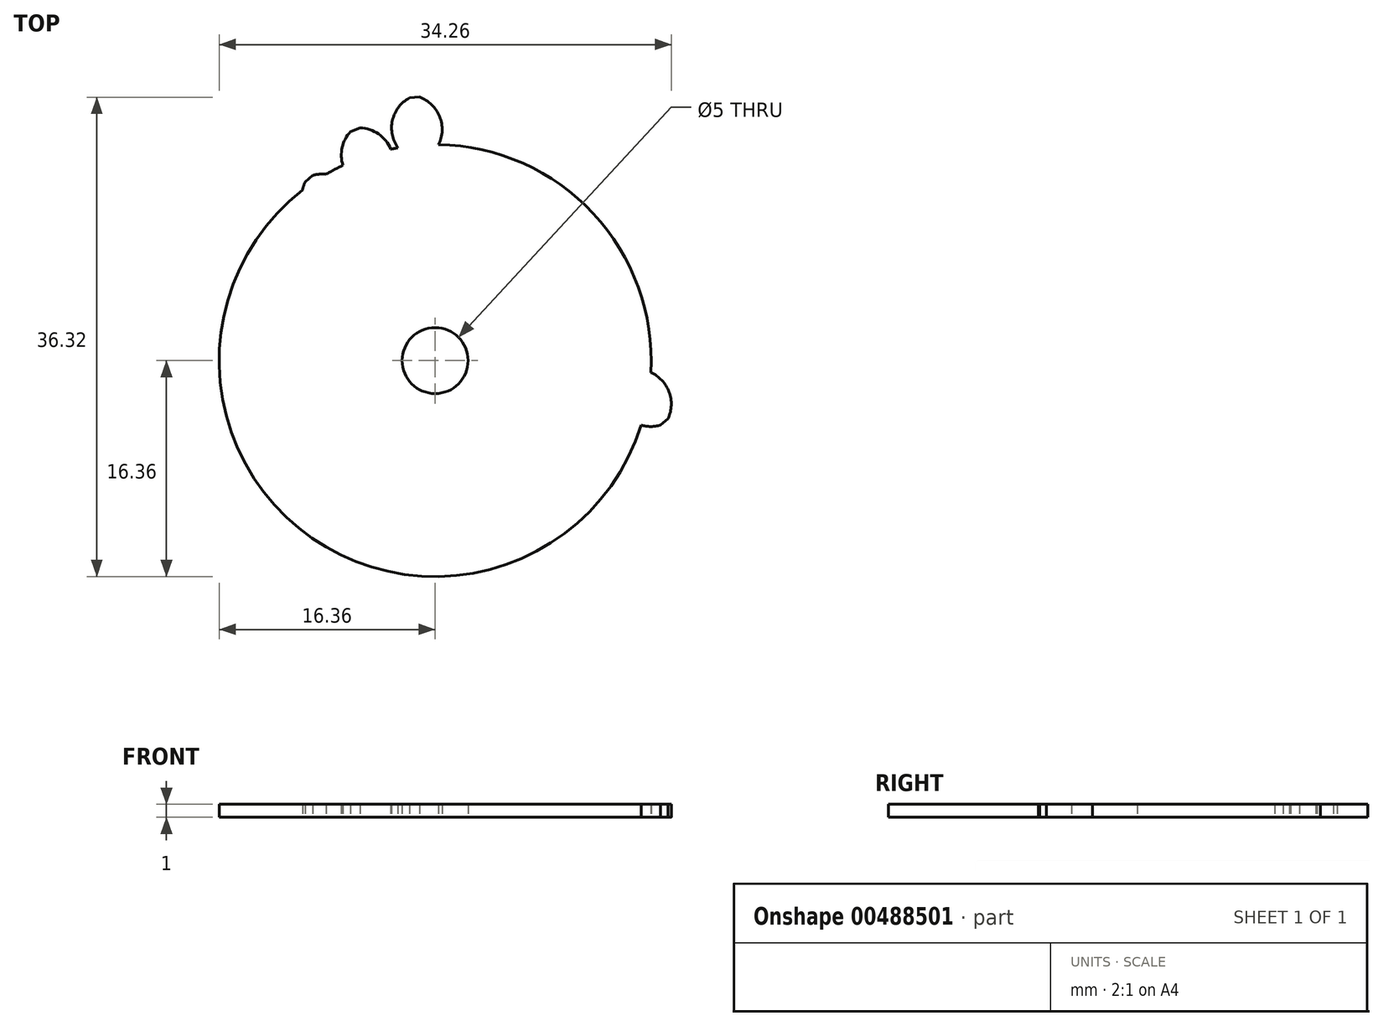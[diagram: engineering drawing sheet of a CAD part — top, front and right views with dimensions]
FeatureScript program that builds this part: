
annotation { "Feature Type Name" : "Feature", "Feature Type Description" : "" }
export const myFeature = defineFeature(function(context is Context, id is Id, definition is map)
    precondition{}
    {
        {
            assignVariable(context, id + "F0", {"name" : "GearDepth", "anyValue" : 1});
        }
        {
            var Q0;
            Q0=qCreatedBy(makeId("Top.planeOp"),FACE);
            var sketch = newSketch(context, id + "F1", { "sketchPlane" : qUnion([Q0])});
            skCircle(sketch, "E0", {"center": v(0, 0) * mm, "radius": 16.36 * mm});
            skCircle(sketch, "E1", {"center": v(0, 0) * mm, "radius": 18.18 * mm, "construction": true});
            skCircle(sketch, "E2", {"center": v(0, 0) * mm, "radius": 20 * mm, "construction": true});
            skLineSegment(sketch, "E3", {"start": v(0, 0) * mm, "end": v(0, 17.6) * mm, "construction": true});
            skLineSegment(sketch, "E4", {"start": v(0, 0) * mm, "end": v(-1.42, 18) * mm, "construction": true});
            skLineSegment(sketch, "E5", {"start": v(0, 18.18) * mm, "end": v(-10.54, 18.18) * mm, "construction": true});
            skLineSegment(sketch, "E6", {"start": v(0, 18.18) * mm, "end": v(-10.3, 14.44) * mm, "construction": true});
            skCircle(sketch, "E7", {"center": v(0, 18.18) * mm, "radius": 4.55 * mm, "construction": true});
            skCircle(sketch, "E8", {"center": v(-4.27, 16.63) * mm, "radius": 4.55 * mm, "construction": true});
            skArc(sketch, "E9", {"start": v(-8.54, 18.18) * mm, "mid": v(-8.56, 18.12) * mm, "end": v(-8.58, 18.06) * mm});
            skArc(sketch, "E10.trimOffspring", {"start": v(0.27, 16.36) * mm, "mid": v(0.34, 18.49) * mm, "end": v(-1.19, 19.96) * mm});
            skArc(sketch, "E11.MirrorCS", {"start": v(-2.82, 16.12) * mm, "mid": v(-3.23, 18.2) * mm, "end": v(-1.95, 19.9) * mm});
            skLineSegment(sketch, "E12", {"start": v(-1.95, 19.9) * mm, "end": v(-1.19, 19.96) * mm});
            skArc(sketch, "E13.1.0", {"start": v(-3.2, 14.66) * mm, "mid": v(-3.78, 16.7) * mm, "end": v(-5.7, 17.64) * mm});
            skLineSegment(sketch, "E13.1.1", {"start": v(-6.4, 17.34) * mm, "end": v(-5.7, 17.64) * mm});
            skArc(sketch, "E13.1.2", {"start": v(-6.06, 13.47) * mm, "mid": v(-7.1, 15.33) * mm, "end": v(-6.4, 17.34) * mm});
            skArc(sketch, "E13.2.0", {"start": v(-5.97, 11.97) * mm, "mid": v(-7.16, 13.74) * mm, "end": v(-9.26, 14.03) * mm});
            skLineSegment(sketch, "E13.2.1", {"start": v(-9.85, 13.53) * mm, "end": v(-9.26, 14.03) * mm});
            skArc(sketch, "E13.2.2", {"start": v(-8.33, 9.96) * mm, "mid": v(-9.88, 11.4) * mm, "end": v(-9.85, 13.53) * mm});
            skArc(sketch, "E13.3.0", {"start": v(-7.77, 8.56) * mm, "mid": v(-9.45, 9.87) * mm, "end": v(-11.54, 9.5) * mm});
            skLineSegment(sketch, "E13.3.1", {"start": v(-11.94, 8.85) * mm, "end": v(-11.54, 9.5) * mm});
            skArc(sketch, "E13.3.2", {"start": v(-9.4, 5.92) * mm, "mid": v(-11.32, 6.81) * mm, "end": v(-11.94, 8.85) * mm});
            skArc(sketch, "E13.4.0", {"start": v(-8.44, 4.76) * mm, "mid": v(-10.43, 5.48) * mm, "end": v(-12.31, 4.49) * mm});
            skLineSegment(sketch, "E13.4.1", {"start": v(-12.5, 3.74) * mm, "end": v(-12.31, 4.49) * mm});
            skArc(sketch, "E13.4.2", {"start": v(-9.16, 1.74) * mm, "mid": v(-11.27, 2) * mm, "end": v(-12.5, 3.74) * mm});
            skArc(sketch, "E13.5.0", {"start": v(-7.89, 0.93) * mm, "mid": v(-10.01, 1) * mm, "end": v(-11.5, -0.52) * mm});
            skLineSegment(sketch, "E13.5.1", {"start": v(-11.43, -1.29) * mm, "end": v(-11.5, -0.52) * mm});
            skArc(sketch, "E13.5.2", {"start": v(-7.65, -2.16) * mm, "mid": v(-9.73, -2.56) * mm, "end": v(-11.43, -1.29) * mm});
            skArc(sketch, "E13.6.0", {"start": v(-6.19, -2.53) * mm, "mid": v(-8.23, -3.12) * mm, "end": v(-9.17, -5.03) * mm});
            skLineSegment(sketch, "E13.6.1", {"start": v(-8.87, -5.74) * mm, "end": v(-9.17, -5.03) * mm});
            skArc(sketch, "E13.6.2", {"start": v(-5, -5.4) * mm, "mid": v(-6.86, -6.43) * mm, "end": v(-8.87, -5.74) * mm});
            skArc(sketch, "E13.7.0", {"start": v(-3.5, -5.3) * mm, "mid": v(-5.26, -6.5) * mm, "end": v(-5.56, -8.6) * mm});
            skLineSegment(sketch, "E13.7.1", {"start": v(-5.06, -9.18) * mm, "end": v(-5.56, -8.6) * mm});
            skArc(sketch, "E13.7.2", {"start": v(-1.49, -7.66) * mm, "mid": v(-2.94, -9.22) * mm, "end": v(-5.06, -9.18) * mm});
            skArc(sketch, "E13.8.0", {"start": v(-0.09, -7.1) * mm, "mid": v(-1.4, -8.78) * mm, "end": v(-1.03, -10.88) * mm});
            skLineSegment(sketch, "E13.8.1", {"start": v(-0.37, -11.28) * mm, "end": v(-1.03, -10.88) * mm});
            skArc(sketch, "E13.8.2", {"start": v(2.56, -8.73) * mm, "mid": v(1.66, -10.65) * mm, "end": v(-0.37, -11.28) * mm});
            skArc(sketch, "E13.9.0", {"start": v(3.72, -7.77) * mm, "mid": v(2.99, -9.77) * mm, "end": v(3.98, -11.64) * mm});
            skLineSegment(sketch, "E13.9.1", {"start": v(4.73, -11.82) * mm, "end": v(3.98, -11.64) * mm});
            skArc(sketch, "E13.9.2", {"start": v(6.73, -8.5) * mm, "mid": v(6.47, -10.6) * mm, "end": v(4.73, -11.82) * mm});
            skArc(sketch, "E13.10.0", {"start": v(7.54, -7.22) * mm, "mid": v(7.46, -9.35) * mm, "end": v(9, -10.83) * mm});
            skLineSegment(sketch, "E13.10.1", {"start": v(9.76, -10.77) * mm, "end": v(9, -10.83) * mm});
            skArc(sketch, "E13.10.2", {"start": v(10.63, -6.98) * mm, "mid": v(11.04, -9.07) * mm, "end": v(9.76, -10.77) * mm});
            skArc(sketch, "E13.11.0", {"start": v(11, -5.52) * mm, "mid": v(11.59, -7.57) * mm, "end": v(13.5, -8.5) * mm});
            skLineSegment(sketch, "E13.11.1", {"start": v(14.2, -8.2) * mm, "end": v(13.5, -8.5) * mm});
            skArc(sketch, "E13.11.2", {"start": v(13.87, -4.34) * mm, "mid": v(14.9, -6.2) * mm, "end": v(14.2, -8.2) * mm});
            skArc(sketch, "E13.12.0", {"start": v(13.78, -2.83) * mm, "mid": v(14.96, -4.6) * mm, "end": v(17.07, -4.9) * mm});
            skLineSegment(sketch, "E13.12.1", {"start": v(17.65, -4.4) * mm, "end": v(17.07, -4.9) * mm});
            skArc(sketch, "E13.12.2", {"start": v(16.13, -0.82) * mm, "mid": v(17.69, -2.27) * mm, "end": v(17.65, -4.4) * mm});
            skArc(sketch, "E13.13.0", {"start": v(15.58, 0.58) * mm, "mid": v(17.25, -0.73) * mm, "end": v(19.35, -0.36) * mm});
            skLineSegment(sketch, "E13.13.1", {"start": v(19.75, 0.3) * mm, "end": v(19.35, -0.36) * mm});
            skArc(sketch, "E13.13.2", {"start": v(17.2, 3.22) * mm, "mid": v(19.13, 2.33) * mm, "end": v(19.75, 0.3) * mm});
            skArc(sketch, "E13.14.0", {"start": v(16.24, 4.38) * mm, "mid": v(18.24, 3.65) * mm, "end": v(20.12, 4.65) * mm});
            skLineSegment(sketch, "E13.14.1", {"start": v(20.3, 5.4) * mm, "end": v(20.12, 4.65) * mm});
            skArc(sketch, "E13.14.2", {"start": v(16.96, 7.4) * mm, "mid": v(19.08, 7.14) * mm, "end": v(20.3, 5.4) * mm});
            skArc(sketch, "E13.15.0", {"start": v(15.7, 8.2) * mm, "mid": v(17.82, 8.13) * mm, "end": v(19.3, 9.66) * mm});
            skLineSegment(sketch, "E13.15.1", {"start": v(19.24, 10.42) * mm, "end": v(19.3, 9.66) * mm});
            skArc(sketch, "E13.15.2", {"start": v(15.45, 11.3) * mm, "mid": v(17.54, 11.7) * mm, "end": v(19.24, 10.42) * mm});
            skArc(sketch, "E13.16.0", {"start": v(14, 11.67) * mm, "mid": v(16.04, 12.26) * mm, "end": v(16.97, 14.17) * mm});
            skLineSegment(sketch, "E13.16.1", {"start": v(16.68, 14.88) * mm, "end": v(16.97, 14.17) * mm});
            skArc(sketch, "E13.16.2", {"start": v(12.8, 14.53) * mm, "mid": v(14.67, 15.57) * mm, "end": v(16.68, 14.88) * mm});
            skArc(sketch, "E13.17.0", {"start": v(11.3, 14.44) * mm, "mid": v(13.07, 15.63) * mm, "end": v(13.37, 17.74) * mm});
            skLineSegment(sketch, "E13.17.1", {"start": v(12.87, 18.32) * mm, "end": v(13.37, 17.74) * mm});
            skArc(sketch, "E13.17.2", {"start": v(9.3, 16.8) * mm, "mid": v(10.74, 18.36) * mm, "end": v(12.87, 18.32) * mm});
            skArc(sketch, "E13.18.0", {"start": v(7.9, 16.25) * mm, "mid": v(9.2, 17.92) * mm, "end": v(8.84, 20.02) * mm});
            skLineSegment(sketch, "E13.18.1", {"start": v(8.18, 20.42) * mm, "end": v(8.84, 20.02) * mm});
            skArc(sketch, "E13.18.2", {"start": v(5.25, 17.87) * mm, "mid": v(6.15, 19.8) * mm, "end": v(8.18, 20.42) * mm});
            skArc(sketch, "E13.19.0", {"start": v(4.09, 16.9) * mm, "mid": v(4.82, 18.9) * mm, "end": v(3.82, 20.78) * mm});
            skLineSegment(sketch, "E13.19.1", {"start": v(3.07, 20.96) * mm, "end": v(3.82, 20.78) * mm});
            skArc(sketch, "E13.19.2", {"start": v(1.08, 17.63) * mm, "mid": v(1.33, 19.74) * mm, "end": v(3.07, 20.96) * mm});
            skPoint(sketch, "E13.center", {"position": v(3.9, 4.57) * mm});
            skCircle(sketch, "E14", {"center": v(0, 0) * mm, "radius": 2.5 * mm});
            skSolve(sketch);
        }
        {
            var Q0;
            {var subQ0=sQuery(id+"F1.wireOp",EDGE,"E10.trimOffspring");Q0=makeQuery(id+"F1.imprint","IMPRINT",FACE,{"disambiguationData":[TD([[makeQuery(id+"F1.imprint","IMPRINT",EDGE,{"derivedFrom":subQ0}),1.0]])]});}
            var Q1;
            {var subQ0=sQuery(id+"F1.wireOp",EDGE,"E0");var subQ1=makeQuery(id+"F1.imprint","INTERSECT",VERTEX,{"derivedFrom":[subQ0,sQuery(id+"F1.wireOp",EDGE,"E10.trimOffspring")]});Q1=makeQuery(id+"F1.imprint","IMPRINT",FACE,{"disambiguationData":[TD([[makeQuery(id+"F1.imprint","IMPRINT",EDGE,{"disambiguationData":[TD([[subQ1,-1.0]])],"derivedFrom":subQ0}),1.0]])]});}
            var Q2;
            {var subQ0=sQuery(id+"F1.wireOp",EDGE,"E13.1.0");Q2=makeQuery(id+"F1.imprint","IMPRINT",FACE,{"disambiguationData":[TD([[makeQuery(id+"F1.imprint","IMPRINT",EDGE,{"derivedFrom":subQ0}),1.0]])]});}
            var Q3;
            {var subQ0=sQuery(id+"F1.wireOp",EDGE,"E13.2.0");Q3=makeQuery(id+"F1.imprint","IMPRINT",FACE,{"disambiguationData":[TD([[makeQuery(id+"F1.imprint","IMPRINT",EDGE,{"derivedFrom":subQ0}),1.0]])]});}
            var Q4;
            {var subQ0=sQuery(id+"F1.wireOp",EDGE,"E13.3.0");Q4=makeQuery(id+"F1.imprint","IMPRINT",FACE,{"disambiguationData":[TD([[makeQuery(id+"F1.imprint","IMPRINT",EDGE,{"derivedFrom":subQ0}),1.0]])]});}
            var Q5;
            {var subQ0=sQuery(id+"F1.wireOp",EDGE,"E13.4.0");Q5=makeQuery(id+"F1.imprint","IMPRINT",FACE,{"disambiguationData":[TD([[makeQuery(id+"F1.imprint","IMPRINT",EDGE,{"derivedFrom":subQ0}),1.0]])]});}
            var Q6;
            {var subQ0=sQuery(id+"F1.wireOp",EDGE,"E13.5.0");Q6=makeQuery(id+"F1.imprint","IMPRINT",FACE,{"disambiguationData":[TD([[makeQuery(id+"F1.imprint","IMPRINT",EDGE,{"derivedFrom":subQ0}),1.0]])]});}
            var Q7;
            {var subQ0=sQuery(id+"F1.wireOp",EDGE,"E13.6.0");Q7=makeQuery(id+"F1.imprint","IMPRINT",FACE,{"disambiguationData":[TD([[makeQuery(id+"F1.imprint","IMPRINT",EDGE,{"derivedFrom":subQ0}),1.0]])]});}
            var Q8;
            {var subQ0=sQuery(id+"F1.wireOp",EDGE,"E13.7.0");Q8=makeQuery(id+"F1.imprint","IMPRINT",FACE,{"disambiguationData":[TD([[makeQuery(id+"F1.imprint","IMPRINT",EDGE,{"derivedFrom":subQ0}),1.0]])]});}
            var Q9;
            {var subQ0=sQuery(id+"F1.wireOp",EDGE,"E13.8.0");Q9=makeQuery(id+"F1.imprint","IMPRINT",FACE,{"disambiguationData":[TD([[makeQuery(id+"F1.imprint","IMPRINT",EDGE,{"derivedFrom":subQ0}),1.0]])]});}
            var Q10;
            {var subQ0=sQuery(id+"F1.wireOp",EDGE,"E13.9.0");Q10=makeQuery(id+"F1.imprint","IMPRINT",FACE,{"disambiguationData":[TD([[makeQuery(id+"F1.imprint","IMPRINT",EDGE,{"derivedFrom":subQ0}),1.0]])]});}
            var Q11;
            {var subQ0=sQuery(id+"F1.wireOp",EDGE,"E13.10.0");Q11=makeQuery(id+"F1.imprint","IMPRINT",FACE,{"disambiguationData":[TD([[makeQuery(id+"F1.imprint","IMPRINT",EDGE,{"derivedFrom":subQ0}),1.0]])]});}
            var Q12;
            {var subQ0=sQuery(id+"F1.wireOp",EDGE,"E13.11.0");Q12=makeQuery(id+"F1.imprint","IMPRINT",FACE,{"disambiguationData":[TD([[makeQuery(id+"F1.imprint","IMPRINT",EDGE,{"derivedFrom":subQ0}),1.0]])]});}
            var Q13;
            {var subQ0=sQuery(id+"F1.wireOp",EDGE,"E13.12.0");Q13=makeQuery(id+"F1.imprint","IMPRINT",FACE,{"disambiguationData":[TD([[makeQuery(id+"F1.imprint","IMPRINT",EDGE,{"derivedFrom":subQ0}),1.0]])]});}
            var Q14;
            {var subQ0=sQuery(id+"F1.wireOp",EDGE,"E13.13.0");Q14=makeQuery(id+"F1.imprint","IMPRINT",FACE,{"disambiguationData":[TD([[makeQuery(id+"F1.imprint","IMPRINT",EDGE,{"derivedFrom":subQ0}),1.0]])]});}
            var Q15;
            {var subQ0=sQuery(id+"F1.wireOp",EDGE,"E13.14.0");Q15=makeQuery(id+"F1.imprint","IMPRINT",FACE,{"disambiguationData":[TD([[makeQuery(id+"F1.imprint","IMPRINT",EDGE,{"derivedFrom":subQ0}),1.0]])]});}
            var Q16;
            {var subQ0=sQuery(id+"F1.wireOp",EDGE,"E13.15.0");Q16=makeQuery(id+"F1.imprint","IMPRINT",FACE,{"disambiguationData":[TD([[makeQuery(id+"F1.imprint","IMPRINT",EDGE,{"derivedFrom":subQ0}),1.0]])]});}
            var Q17;
            {var subQ0=sQuery(id+"F1.wireOp",EDGE,"E13.16.0");Q17=makeQuery(id+"F1.imprint","IMPRINT",FACE,{"disambiguationData":[TD([[makeQuery(id+"F1.imprint","IMPRINT",EDGE,{"derivedFrom":subQ0}),1.0]])]});}
            var Q18;
            {var subQ0=sQuery(id+"F1.wireOp",EDGE,"E13.17.0");Q18=makeQuery(id+"F1.imprint","IMPRINT",FACE,{"disambiguationData":[TD([[makeQuery(id+"F1.imprint","IMPRINT",EDGE,{"derivedFrom":subQ0}),1.0]])]});}
            var Q19;
            {var subQ0=sQuery(id+"F1.wireOp",EDGE,"E13.18.0");Q19=makeQuery(id+"F1.imprint","IMPRINT",FACE,{"disambiguationData":[TD([[makeQuery(id+"F1.imprint","IMPRINT",EDGE,{"derivedFrom":subQ0}),1.0]])]});}
            var Q20;
            {var subQ0=sQuery(id+"F1.wireOp",EDGE,"E13.19.0");Q20=makeQuery(id+"F1.imprint","IMPRINT",FACE,{"disambiguationData":[TD([[makeQuery(id+"F1.imprint","IMPRINT",EDGE,{"derivedFrom":subQ0}),1.0]])]});}
            var Q21;
            Q21=sQuery(id+"F1.wireOp",EDGE,"E0");
            var Q22;
            Q22=sQuery(id+"F1.wireOp",EDGE,"E10.trimOffspring");
            var Q23;
            Q23=sQuery(id+"F1.wireOp",EDGE,"E12");
            var Q24;
            Q24=sQuery(id+"F1.wireOp",EDGE,"E11.MirrorCS");
            extrude(context, id + "F2", {"entities" : qUnion([Q0, Q1, Q2, Q3, Q4, Q5, Q6, Q7, Q8, Q9, Q10, Q11, Q12, Q13, Q14, Q15, Q16, Q17, Q18, Q19, Q20]), "surfaceEntities" : qUnion([Q21, Q22, Q23, Q24]), "depth" : (getVariable(context, 'GearDepth')) * mm});
        }
    });
